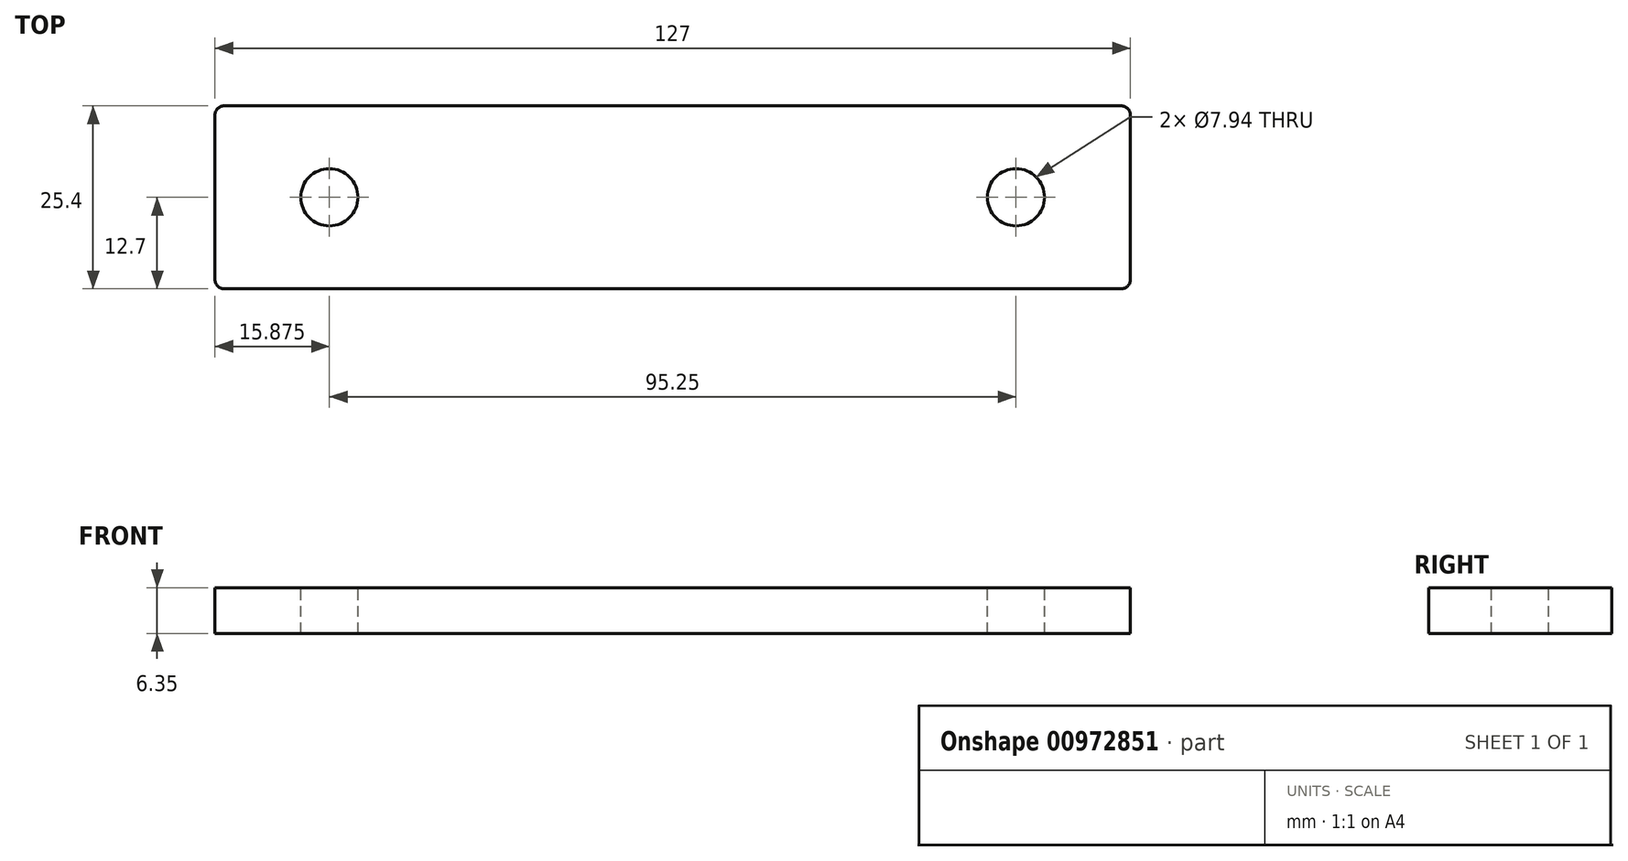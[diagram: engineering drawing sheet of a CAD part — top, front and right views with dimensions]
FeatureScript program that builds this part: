
annotation { "Feature Type Name" : "Feature", "Feature Type Description" : "" }
export const myFeature = defineFeature(function(context is Context, id is Id, definition is map)
    precondition{}
    {
        {
            var Q0;
            Q0=qCreatedBy(makeId("Top.planeOp"),FACE);
            var sketch = newSketch(context, id + "F0", { "sketchPlane" : qUnion([Q0])});
            skLineSegment(sketch, "E0.bottom", {"start": v(63.5, 12.7) * mm, "end": v(-63.5, 12.7) * mm});
            skLineSegment(sketch, "E0.top", {"start": v(63.5, -12.7) * mm, "end": v(-63.5, -12.7) * mm});
            skLineSegment(sketch, "E0.left", {"start": v(63.5, 12.7) * mm, "end": v(63.5, -12.7) * mm});
            skLineSegment(sketch, "E0.right", {"start": v(-63.5, 12.7) * mm, "end": v(-63.5, -12.7) * mm});
            skPoint(sketch, "E0.middle", {"position": v(0, 0) * mm});
            skSolve(sketch);
        }
        {
            var Q0;
            Q0 = qSketchRegion(id + "F0", true);
            extrude(context, id + "F1", {"entities" : qUnion([Q0]), "oppositeDirection" : true, "depth" : 6.35 * mm, "offsetDistance" : 25.4 * mm});
        }
        {
            var Q0;
            Q0=makeQuery(id+"F1.opExtrude","SWEPT_EDGE",EDGE,{"disambiguationData":[OSD([sQuery(id+"F0.wireOp",EDGE,"E0.top"),sQuery(id+"F0.wireOp",EDGE,"E0.right")])]});
            var Q1;
            Q1=makeQuery(id+"F1.opExtrude","SWEPT_EDGE",EDGE,{"disambiguationData":[OSD([sQuery(id+"F0.wireOp",EDGE,"E0.bottom"),sQuery(id+"F0.wireOp",EDGE,"E0.right")])]});
            var Q2;
            Q2=makeQuery(id+"F1.opExtrude","SWEPT_EDGE",EDGE,{"disambiguationData":[OSD([sQuery(id+"F0.wireOp",EDGE,"E0.bottom"),sQuery(id+"F0.wireOp",EDGE,"E0.left")])]});
            var Q3;
            Q3=makeQuery(id+"F1.opExtrude","SWEPT_EDGE",EDGE,{"disambiguationData":[OSD([sQuery(id+"F0.wireOp",EDGE,"E0.top"),sQuery(id+"F0.wireOp",EDGE,"E0.left")])]});
            fillet(context, id + "F2", {"entities" : qUnion([Q0, Q1, Q2, Q3]), "radius" : 1.27 * mm, "tangentPropagation" : true, "allowEdgeOverflow" : false});
        }
        {
            var Q0;
            Q0=makeQuery(id+"F1.opExtrude","CAP_FACE",FACE,{"disambiguationData":[OSD([sQuery(id+"F0.wireOp",EDGE,"E0.bottom"),sQuery(id+"F0.wireOp",EDGE,"E0.top"),sQuery(id+"F0.wireOp",EDGE,"E0.left"),sQuery(id+"F0.wireOp",EDGE,"E0.right")])],"isStart":true});
            var sketch = newSketch(context, id + "F3", { "sketchPlane" : qUnion([Q0])});
            skPoint(sketch, "E1", {"position": v(-47.62, 0) * mm});
            skPoint(sketch, "E2", {"position": v(47.62, 0) * mm});
            skSolve(sketch);
        }
        {
            var Q0;
            Q0=sQuery(id+"F3.wireOp",VERTEX,"E1");
            var Q1;
            Q1=sQuery(id+"F3.wireOp",VERTEX,"E2");
            var Q2;
            Q2=makeQuery(id+"F1.opExtrude","SWEPT_BODY",BODY,{"disambiguationData":[OSD([sQuery(id+"F0.wireOp",EDGE,"E0.bottom"),sQuery(id+"F0.wireOp",EDGE,"E0.top"),sQuery(id+"F0.wireOp",EDGE,"E0.left"),sQuery(id+"F0.wireOp",EDGE,"E0.right")])]});
            hole(context, id + "F4", {"style" : HoleStyle.SIMPLE, "endStyle" : HoleEndStyle.THROUGH, "holeDiameter" : 7.94 * mm, "majorDiameter" : 6.35 * mm, "tappedDepth" : 12.7 * mm, "tapClearance" : 3, "locations" : qUnion([Q0, Q1]), "scope" : qUnion([Q2])});
        }
    });
